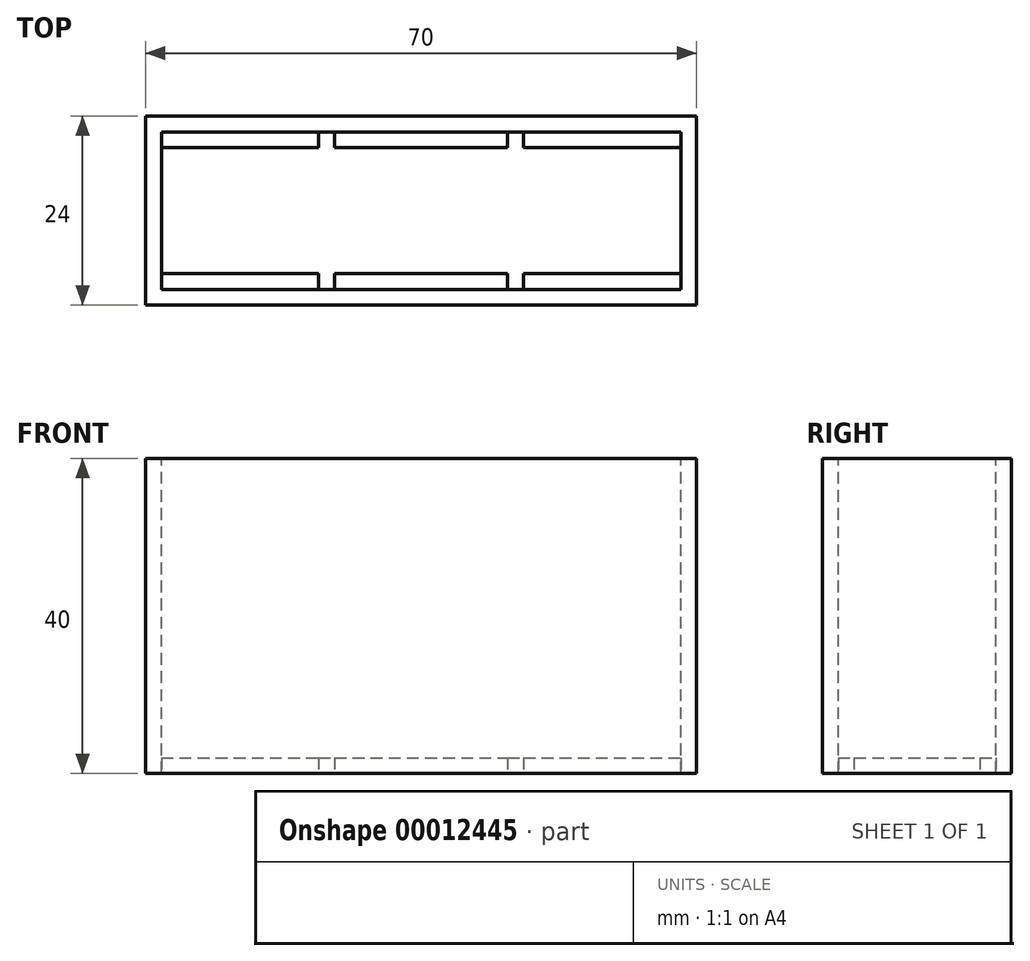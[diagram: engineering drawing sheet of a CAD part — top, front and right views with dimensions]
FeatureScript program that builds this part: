
annotation { "Feature Type Name" : "Feature", "Feature Type Description" : "" }
export const myFeature = defineFeature(function(context is Context, id is Id, definition is map)
    precondition{}
    {
        {
            var Q0;
            Q0=qCreatedBy(makeId("Front.planeOp"),FACE);
            var sketch = newSketch(context, id + "F0", { "sketchPlane" : qUnion([Q0])});
            skLineSegment(sketch, "E0.bottom", {"start": v(0, 0) * mm, "end": v(-70, 0) * mm});
            skLineSegment(sketch, "E0.left", {"start": v(0, 0) * mm, "end": v(0, 40) * mm});
            skLineSegment(sketch, "E0.right", {"start": v(-70, 0) * mm, "end": v(-70, 40) * mm});
            skPoint(sketch, "E1.visualSharp", {"position": v(0, 40) * mm});
            skLineSegment(sketch, "E1.filletArc", {"start": v(0, 40) * mm, "end": v(0, 40) * mm});
            skPoint(sketch, "E2.visualSharp", {"position": v(-70, 40) * mm});
            skLineSegment(sketch, "E2.filletArc", {"start": v(-70, 40) * mm, "end": v(-70, 40) * mm});
            skLineSegment(sketch, "E3", {"start": v(-70, 40) * mm, "end": v(0, 40) * mm});
            skSolve(sketch);
        }
        {
            var Q0;
            Q0=qSketchRegion(id+"F0",true);
            extrude(context, id + "F1", {"entities" : qUnion([Q0]), "oppositeDirection" : true, "depth" : 2 * mm});
        }
        {
            var Q0;
            Q0=makeQuery(id+"F1.opExtrude","CAP_FACE",FACE,{"disambiguationData":[OSD([sQuery(id+"F0.wireOp",EDGE,"E0.bottom"),sQuery(id+"F0.wireOp",EDGE,"E0.top"),sQuery(id+"F0.wireOp",EDGE,"E0.left"),sQuery(id+"F0.wireOp",EDGE,"E0.right")])],"isStart":true});
            var sketch = newSketch(context, id + "F2", { "sketchPlane" : qUnion([Q0])});
            skLineSegment(sketch, "E4.bottom", {"start": v(-70, 2) * mm, "end": v(0, 2) * mm});
            skLineSegment(sketch, "E4.top", {"start": v(-70, 0) * mm, "end": v(0, 0) * mm});
            skLineSegment(sketch, "E4.left", {"start": v(-70, 2) * mm, "end": v(-70, 0) * mm});
            skLineSegment(sketch, "E4.right", {"start": v(0, 2) * mm, "end": v(0, 0) * mm});
            skLineSegment(sketch, "E5.bottom", {"start": v(0, 2) * mm, "end": v(-2, 2) * mm});
            skLineSegment(sketch, "E5.top", {"start": v(0, 40) * mm, "end": v(-2, 40) * mm});
            skLineSegment(sketch, "E5.left", {"start": v(0, 2) * mm, "end": v(0, 40) * mm});
            skLineSegment(sketch, "E5.right", {"start": v(-2, 2) * mm, "end": v(-2, 40) * mm});
            skLineSegment(sketch, "E6.bottom", {"start": v(-70, 2) * mm, "end": v(-68, 2) * mm});
            skLineSegment(sketch, "E6.top", {"start": v(-70, 40) * mm, "end": v(-68, 40) * mm});
            skLineSegment(sketch, "E6.left", {"start": v(-70, 2) * mm, "end": v(-70, 40) * mm});
            skLineSegment(sketch, "E6.right", {"start": v(-68, 2) * mm, "end": v(-68, 40) * mm});
            skSolve(sketch);
        }
        {
            var Q0;
            Q0=qSketchRegion(id+"F2",true);
            extrude(context, id + "F3", {"entities" : qUnion([Q0]), "operationType" : NewBodyOperationType.ADD, "depth" : 20 * mm});
        }
        {
            var Q0;
            Q0=makeQuery(id+"F3.opExtrude","CAP_FACE",FACE,{"disambiguationData":[OSD([sQuery(id+"F2.wireOp",EDGE,"E4.bottom"),sQuery(id+"F2.wireOp",EDGE,"E4.top"),sQuery(id+"F2.wireOp",EDGE,"E4.left"),sQuery(id+"F2.wireOp",EDGE,"E4.right"),sQuery(id+"F2.wireOp",EDGE,"E5.top"),sQuery(id+"F2.wireOp",EDGE,"E5.left"),sQuery(id+"F2.wireOp",EDGE,"E5.right"),sQuery(id+"F2.wireOp",EDGE,"E6.top"),sQuery(id+"F2.wireOp",EDGE,"E6.left"),sQuery(id+"F2.wireOp",EDGE,"E6.right"),sQuery(id+"F2.wireOp",EDGE,"de096a0c-0b75-4910-984c-67acd1122c40.bottom"),sQuery(id+"F2.wireOp",EDGE,"de096a0c-0b75-4910-984c-67acd1122c40.left"),sQuery(id+"F2.wireOp",EDGE,"de096a0c-0b75-4910-984c-67acd1122c40.right"),sQuery(id+"F2.wireOp",EDGE,"aab91a0f-a239-46ca-9d51-01bc5ff683ef.bottom"),sQuery(id+"F2.wireOp",EDGE,"aab91a0f-a239-46ca-9d51-01bc5ff683ef.left"),sQuery(id+"F2.wireOp",EDGE,"aab91a0f-a239-46ca-9d51-01bc5ff683ef.right"),sQuery(id+"F2.wireOp",EDGE,"2607705c-8984-4d33-aef6-461a68198688.bottom"),sQuery(id+"F2.wireOp",EDGE,"2607705c-8984-4d33-aef6-461a68198688.left"),sQuery(id+"F2.wireOp",EDGE,"2607705c-8984-4d33-aef6-461a68198688.right"),sQuery(id+"F2.wireOp",EDGE,"6ecffad1-5da9-418b-b4c0-dc3906f63474.bottom"),sQuery(id+"F2.wireOp",EDGE,"6ecffad1-5da9-418b-b4c0-dc3906f63474.left"),sQuery(id+"F2.wireOp",EDGE,"6ecffad1-5da9-418b-b4c0-dc3906f63474.right")])],"isStart":false});
            var sketch = newSketch(context, id + "F4", { "sketchPlane" : qUnion([Q0])});
            skLineSegment(sketch, "E7.bottom", {"start": v(-70, 0) * mm, "end": v(0, 0) * mm});
            skLineSegment(sketch, "E7.top", {"start": v(-70, 40) * mm, "end": v(0, 40) * mm});
            skLineSegment(sketch, "E7.left", {"start": v(-70, 0) * mm, "end": v(-70, 40) * mm});
            skLineSegment(sketch, "E7.right", {"start": v(0, 0) * mm, "end": v(0, 40) * mm});
            skSolve(sketch);
        }
        {
            var Q0;
            Q0=qSketchRegion(id+"F4",true);
            extrude(context, id + "F5", {"entities" : qUnion([Q0]), "operationType" : NewBodyOperationType.ADD, "depth" : 2 * mm});
        }
        {
            var Q0;
            Q0=makeQuery(id+"F5.boolean.opBoolean","MERGE",FACE,{"derivedFrom":[makeQuery(id+"F3.boolean.opBoolean","MERGE",FACE,{"derivedFrom":[makeQuery(id+"F1.opExtrude","SWEPT_FACE",FACE,{"disambiguationData":[OSD([sQuery(id+"F0.wireOp",EDGE,"E0.bottom")])]}),makeQuery(id+"F3.opExtrude","SWEPT_FACE",FACE,{"disambiguationData":[OSD([sQuery(id+"F2.wireOp",EDGE,"E4.top")])]})]}),makeQuery(id+"F5.opExtrude","SWEPT_FACE",FACE,{"disambiguationData":[OSD([sQuery(id+"F4.wireOp",EDGE,"E7.bottom")])]})]});
            var sketch = newSketch(context, id + "F6", { "sketchPlane" : qUnion([Q0])});
            skLineSegment(sketch, "E8.bottom", {"start": v(-68, 0) * mm, "end": v(-48, 0) * mm});
            skLineSegment(sketch, "E8.top", {"start": v(-68, 2) * mm, "end": v(-48, 2) * mm});
            skLineSegment(sketch, "E8.left", {"start": v(-68, 0) * mm, "end": v(-68, 2) * mm});
            skLineSegment(sketch, "E8.right", {"start": v(-48, 0) * mm, "end": v(-48, 2) * mm});
            skLineSegment(sketch, "E9.bottom", {"start": v(-46, 0) * mm, "end": v(-24, 0) * mm});
            skLineSegment(sketch, "E9.top", {"start": v(-46, 2) * mm, "end": v(-24, 2) * mm});
            skLineSegment(sketch, "E9.left", {"start": v(-46, 0) * mm, "end": v(-46, 2) * mm});
            skLineSegment(sketch, "E9.right", {"start": v(-24, 0) * mm, "end": v(-24, 2) * mm});
            skLineSegment(sketch, "E10.bottom", {"start": v(-22, 0) * mm, "end": v(-2, 0) * mm});
            skLineSegment(sketch, "E10.top", {"start": v(-22, 2) * mm, "end": v(-2, 2) * mm});
            skLineSegment(sketch, "E10.left", {"start": v(-22, 0) * mm, "end": v(-22, 2) * mm});
            skLineSegment(sketch, "E10.right", {"start": v(-2, 0) * mm, "end": v(-2, 2) * mm});
            skLineSegment(sketch, "E11.bottom", {"start": v(-2, 18) * mm, "end": v(-22, 18) * mm});
            skLineSegment(sketch, "E11.top", {"start": v(-2, 20) * mm, "end": v(-22, 20) * mm});
            skLineSegment(sketch, "E11.left", {"start": v(-2, 18) * mm, "end": v(-2, 20) * mm});
            skLineSegment(sketch, "E11.right", {"start": v(-22, 18) * mm, "end": v(-22, 20) * mm});
            skLineSegment(sketch, "E12.bottom", {"start": v(-24, 18) * mm, "end": v(-46, 18) * mm});
            skLineSegment(sketch, "E12.top", {"start": v(-24, 20) * mm, "end": v(-46, 20) * mm});
            skLineSegment(sketch, "E12.left", {"start": v(-24, 18) * mm, "end": v(-24, 20) * mm});
            skLineSegment(sketch, "E12.right", {"start": v(-46, 18) * mm, "end": v(-46, 20) * mm});
            skLineSegment(sketch, "E13.bottom", {"start": v(-48, 18) * mm, "end": v(-68, 18) * mm});
            skLineSegment(sketch, "E13.top", {"start": v(-48, 20) * mm, "end": v(-68, 20) * mm});
            skLineSegment(sketch, "E13.left", {"start": v(-48, 18) * mm, "end": v(-48, 20) * mm});
            skLineSegment(sketch, "E13.right", {"start": v(-68, 18) * mm, "end": v(-68, 20) * mm});
            skSolve(sketch);
        }
        {
            var Q0;
            Q0=qSketchRegion(id+"F6",true);
            extrude(context, id + "F7", {"entities" : qUnion([Q0]), "operationType" : NewBodyOperationType.REMOVE, "oppositeDirection" : true, "depth" : 30 * mm});
        }
    });
